# Revit family: Building-FlushMountingEnclosures-GEWISS-48PTC-ENCLOSURES-MODULAR-IP55
name_source: partatom
category: Attrezzatura elettrica
revit_build: Autodesk Revit 2016 (Build: 20161004_0715(x64)
units: mm (PartAtom-declared; Revit-internal decimal feet)

## family parameters
Condiviso = No
Configurazione quadro = Due colonne, circuiti in orizzontale
Host = Muro
Numero OmniClass = 23.60.00.00
Punto di calcolo locali = No
Quota connettore circolare = Usa diametro
Sempre verticale = Sì
Taglio con vuoti quando caricato = No
Tipo di parte = Pannello comandi
Titolo OmniClass = General Purpose: Services

## types (1)
- GW48686 - FLUSH-MOUNT.COMB.ENCL.4M+2FL.IP55 GR7035
    Carico = Altro
    Catalogue = BUILDING
    Catalogue Range = 48 PTC
    Colour = Grey RAL 7035
    Descrizione = FLUSH-MOUNT.COMB.ENCL.4M+2FL.IP55 GR7035
    Dispersible power (W) = 19
    Door colour = Smoked Transparent
    EAN code = 8011564071728
    Electrocod = 1320
    Front dim. LxH (mm) = 345x210
    Glow Wire Test = 650°C
    H_da terra = 922 mm
    IDF = 6d424fe3-a087-4774-ba9e-aea5d60a625b
    IDT = d60fa815-1ed1-451d-83db-3132591f839a
    IP degree = IP55
    Immagine tipo = GW48686.jpg
    Installation = Flush mounting enclosures
    Insulation class = II (according to IEC 61140 standards)
    Lid colour = Grey RAL 7035
    Modello = GW48686
    No. of modules EN 50022 = 4
    Numero di poli = 1
    Operating temperature = -15 ÷ +60°C
    Outer dim. LxHxD (mm) = 308x169x70
    Potenza = 0 V
    Produttore = GEWISS S.p.A.
    SEO = Board
    Shock resistance = IK08
    Technical sheet = https://www.gewiss.com
    Thermo-pressure with ball = 70
    Type of material = Halogen-free in compliance with EN 60754-2
    URL = https://www.gewiss.com
    Version file RFA = 18.0

note: source unit labels omitted for Thermo-pressure with ball — the stored unit's dimension contradicts the parameter name (converter mislabeling)
